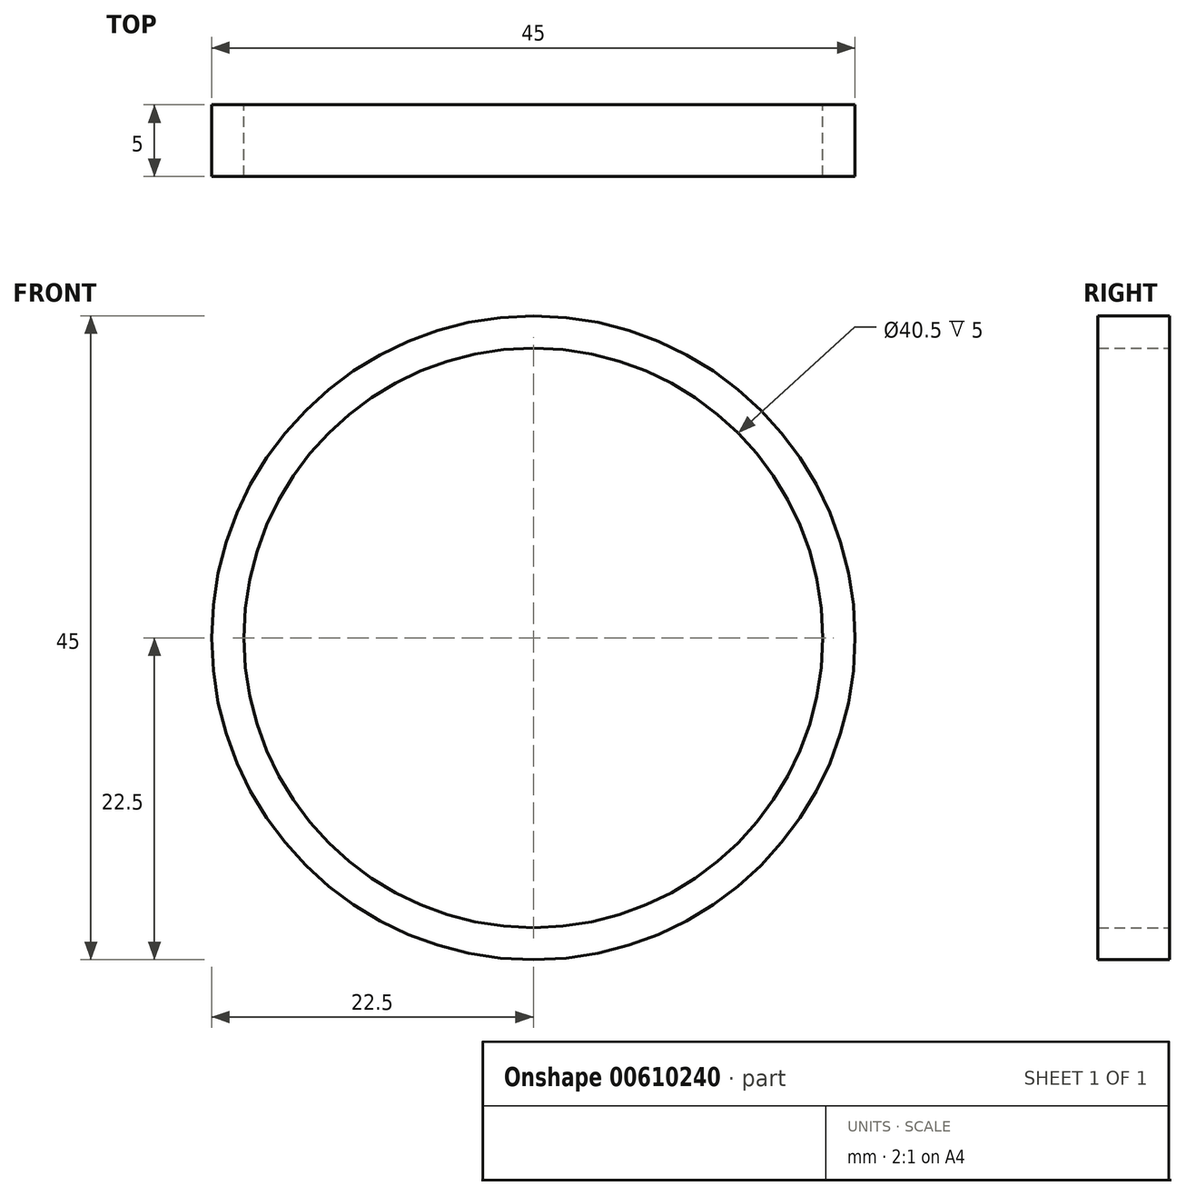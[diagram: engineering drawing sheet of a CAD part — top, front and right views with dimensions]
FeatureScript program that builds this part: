
annotation { "Feature Type Name" : "Feature", "Feature Type Description" : "" }
export const myFeature = defineFeature(function(context is Context, id is Id, definition is map)
    precondition{}
    {
        {
            var Q0;
            Q0=qCreatedBy(makeId("Front.planeOp"),FACE);
            var sketch = newSketch(context, id + "F0", { "sketchPlane" : qUnion([Q0])});
            skCircle(sketch, "E0", {"center": v(0, 0) * mm, "radius": 20.25 * mm});
            skCircle(sketch, "E1", {"center": v(0, 0) * mm, "radius": 22.5 * mm});
            skSolve(sketch);
        }
        {
            var Q0;
            Q0=makeQuery(id+"F0.imprint","IMPRINT",FACE,{"disambiguationData":[TD([[makeQuery(id+"F0.imprint","IMPRINT",EDGE,{"derivedFrom":sQuery(id+"F0.wireOp",EDGE,"E0")}),-1.0]])]});
            extrude(context, id + "F1", {"entities" : qUnion([Q0]), "depth" : 5 * mm, "offsetDistance" : 25 * mm});
        }
    });
